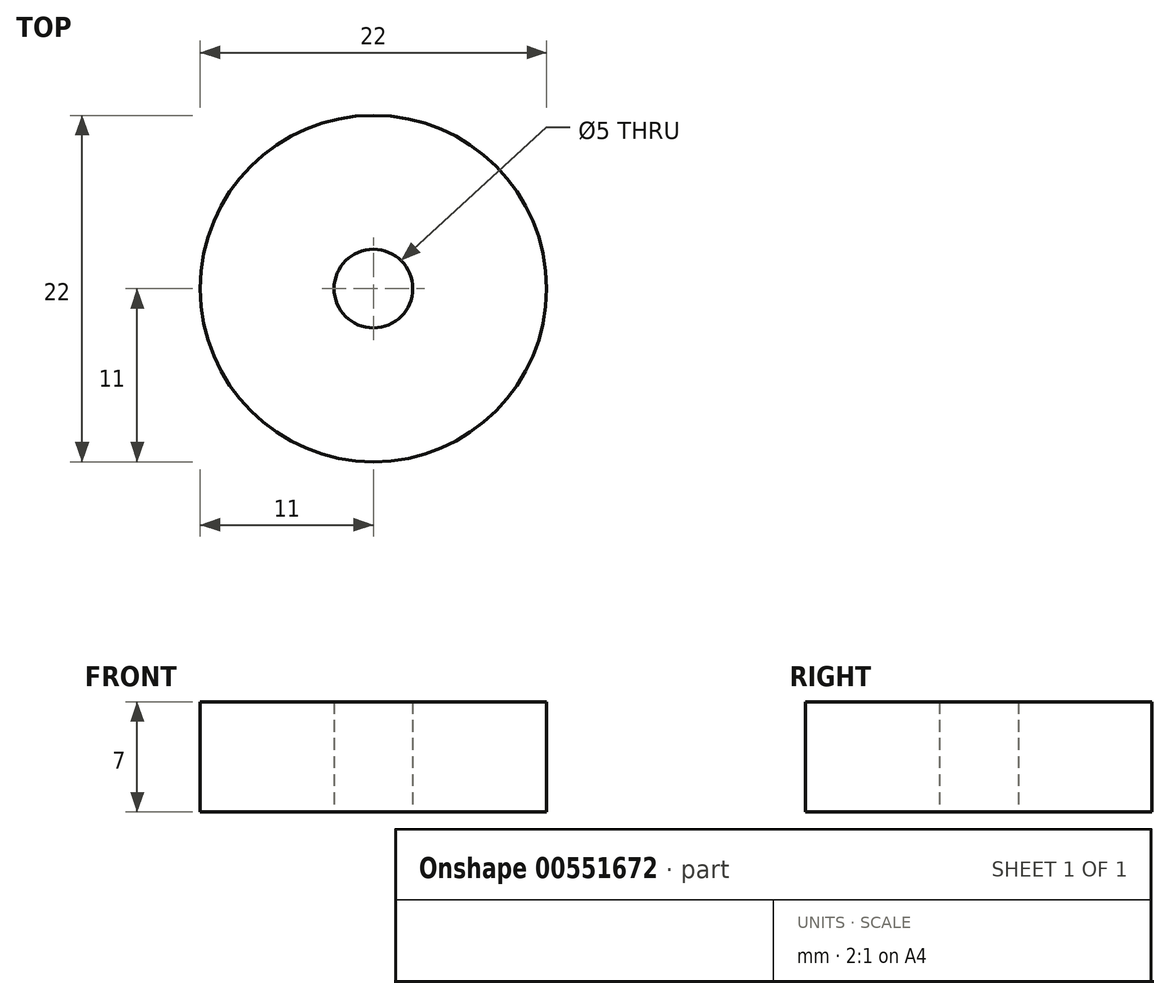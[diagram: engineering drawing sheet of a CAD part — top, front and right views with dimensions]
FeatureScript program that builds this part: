
annotation { "Feature Type Name" : "Feature", "Feature Type Description" : "" }
export const myFeature = defineFeature(function(context is Context, id is Id, definition is map)
    precondition{}
    {
        {
            var Q0;
            Q0=qCreatedBy(makeId("Top.planeOp"),FACE);
            var sketch = newSketch(context, id + "F0", { "sketchPlane" : qUnion([Q0])});
            skCircle(sketch, "E0", {"center": v(0, 0) * mm, "radius": 11 * mm});
            skCircle(sketch, "E1", {"center": v(0, 0) * mm, "radius": 2.5 * mm});
            skSolve(sketch);
        }
        {
            var Q0;
            Q0=qSketchRegion(id+"F0",true);
            extrude(context, id + "F1", {"entities" : qUnion([Q0]), "depth" : 7 * mm, "offsetDistance" : 25 * mm});
        }
    });
